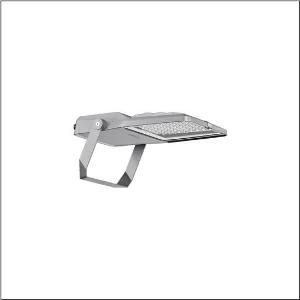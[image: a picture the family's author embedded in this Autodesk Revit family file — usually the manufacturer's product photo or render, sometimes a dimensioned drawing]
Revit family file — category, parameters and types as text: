
# Revit family: floodlight_fl_21_iq_mini___pl52_5xa7772d2d1a_b3d3
name_source: partatom
category: Lighting Fixtures
units: mm (PartAtom-declared; Revit-internal decimal feet)

## family parameters
Cut with Voids When Loaded = No
Host = Face
Light Source = No
Part Type = Normal
Room Calculation Point = No
Round Connector Dimension = Use Diameter
Shared = No

## types (1)
- --- (1 x LED, 17830 lm, 143 W, 3000K)
    Apparent Load = 143 VA
    CIE Flux Codes = 26 60 98 100 100
    Color Rendering = 70
    Color Temperature = 3000K
    Default Elevation = 1800 mm
    Description = Floodlight FL 21 iQ mini, floodlight, primary light control with lens, of PMMA, primary optical cover: protective disc, of toughened safety glass, transparent, light distribution: PL52, light emission: direct distribution, installation type: surface-mounted, lamps: LED, High Power LED, rated values: 17.830lm | 143W | 124,7lm/W (begin service life); end service life: 17.830lm | 151,6W; at 50% lumin. flux: 8.915lm | 60,6W | 147,1lm/W, colour temperature: 3000K, colour rendering: CRI > 70, light colour: 730, light setting 1 begin service life: 100% | 17.830lm | 143W | 124,7lm/W | 3.000K, light setting 1 end service life: 151,6W, further light settings possible, control: Street-Remote, Auto-Match, Temp-Guard, Night-Set, Smart-Wire, Desk-Remote (wireless, voltage-free reading and setting of iQ features in the workshop via application-optimized NFC function/RFID function), optimised constant luminous flux control (CLO 2.0), pre-setting: linear dimming characteristic, with terminal, 6-pole, mains connection: 220..240V, AC, 50/60Hz, luminaire housing, of diecast aluminium, powder-coated, SITECO metallic grey (DB 702S), corrosivity category C5 mid according to DIN EN ISO 12944suitable for swimming poolschlorine-resistant, sealing non-destructively replaceable, mounting bracket, of steel, galvanised, powder-coated, SITECO metallic grey (DB 702S), protection rating (complete): IP66, insulation class (complete): insulation class II (safety insulation), certification: CE, ENEC, VDE, protection symbol: D, impact resistance: IK08, permissible operating ambient temperature: -40..+40°C, permissible operating ambient temperature for outdoor applications: -40..+50°C, standard: DIN EN 12944, LABS conformity tested according to VDMA 24364:2018-05, packaging unit: 1 piece

Light Distribution: PL52
    Height = 70 mm
    Lamp = 1 x LED
    Lamp Light Flux = 17830 lm
    Lamp Power = 143 W
    Lamp count = 1
    Length = 485 mm
    Luminous efficacy = 125 lm/W
    Manufacturer = Siteco
    ModVariant = No
    Model = 5XA7772D2D1A
    Mounting Place = Pole
    Mounting Type = Pole annexe
    Number of Poles = 1
    OnlyDefault = Yes
    Power Factor = 1
    Product Name = Floodlight FL 21 iQ mini | PL52
    Product group = floodlight | pylon annexe
    ProductGroupID = 6201
    Protection Class = Protection class II
    Protection Degree = IP 66
    RLX_Detail_Level = 1
    RLX_Emergency_Light_Flux = 0 lm
    RLX_Emergency_Type = 0
    RLX_Emergency_Type_DB = No
    RlxData = <blob elided: 97005 chars, md5=998a1eb3>
    Socket = socket
    Standby Power = 0 W
    System Light Flux = 17830 lm
    System Power = 143 W
    Type Comments = factory setting: luminous flux: 100 % | dim-lin: 254 | 730 mA
    Type Image = l_1006845.jpg
    URL = http://relux.com
    VarID = @adj_164813
    Voltage = 0 V
    Weight = 0.00 kg
    Width = 337 mm

## geometry (parser evidence)
native form markers: Blend x4, Sweep x12
no freeform markers — native parametric forms only
